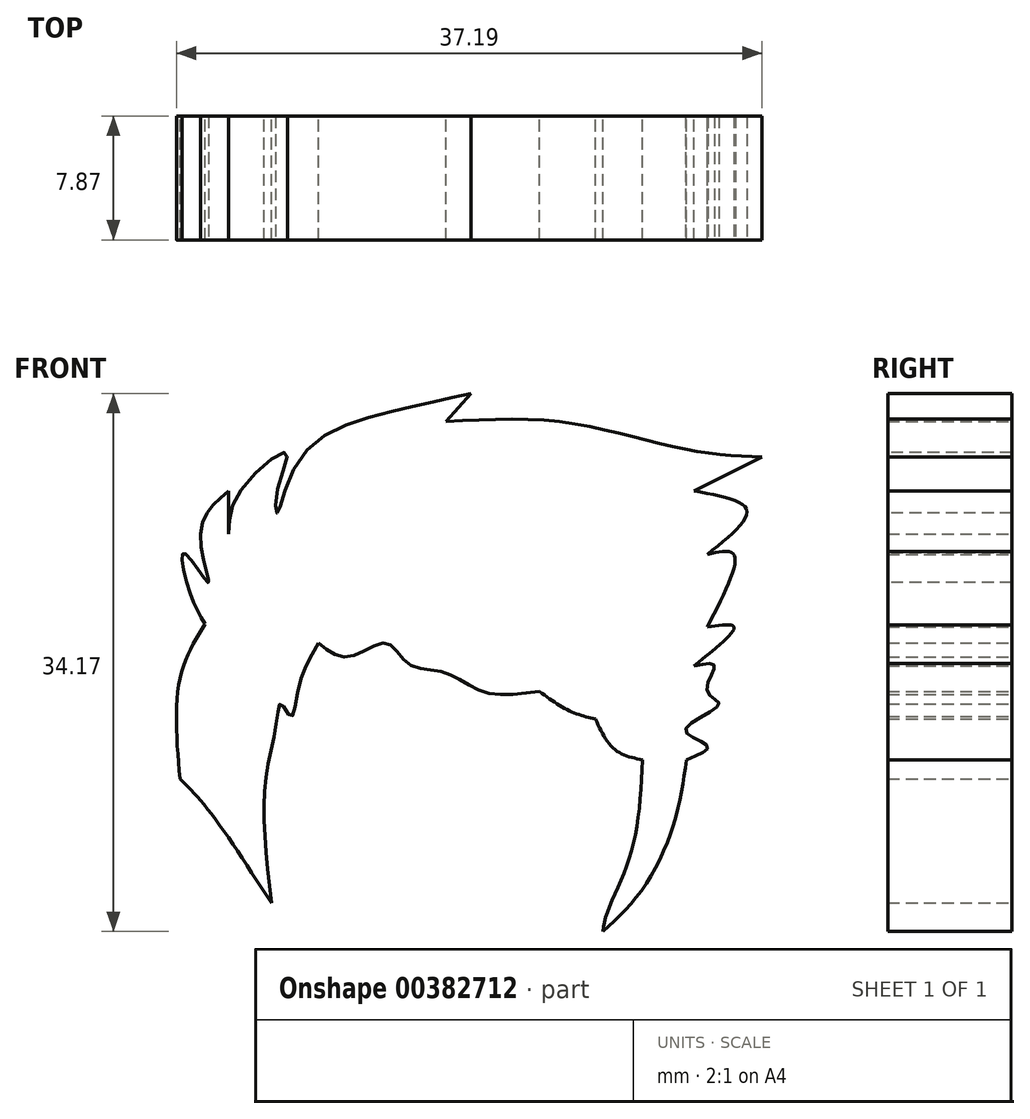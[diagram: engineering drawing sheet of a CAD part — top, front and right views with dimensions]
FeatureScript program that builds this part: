
annotation { "Feature Type Name" : "Feature", "Feature Type Description" : "" }
export const myFeature = defineFeature(function(context is Context, id is Id, definition is map)
    precondition{}
    {
        {
            var Q0;
            Q0=qCreatedBy(makeId("Front.planeOp"),FACE);
            var sketch = newSketch(context, id + "F0", { "sketchPlane" : qUnion([Q0])});
            skFitSpline(sketch, "E0", {"points": [v(-99.37, 25.37) * mm, v(-100.4, 27.63) * mm, v(-100.68, 29.88) * mm, v(-99.18, 28) * mm, v(-99.65, 31) * mm, v(-97.86, 33.82) * mm], "startDerivative": vector(-5.52, 9.55) * mm, "endDerivative": vector(11.78, 9.9) * mm});
            skFitSpline(sketch, "E1", {"points": [v(-97.86, 31.1) * mm, v(-97.86, 33.82) * mm], "startDerivative": vector(0, 2.72) * mm, "endDerivative": vector(0, 2.72) * mm});
            skFitSpline(sketch, "E2", {"points": [v(-97.86, 31.1) * mm, v(-97.11, 33.82) * mm, v(-94.2, 36.26) * mm, v(-94.77, 33.82) * mm, v(-94.77, 32.41) * mm, v(-93.27, 35.98) * mm, v(-87.45, 38.89) * mm, v(-82.48, 40.01) * mm], "startDerivative": vector(0.53, 19.9) * mm, "endDerivative": vector(27.38, 6.02) * mm});
            skFitSpline(sketch, "E3", {"points": [v(-84.07, 38.23) * mm, v(-82.48, 40.01) * mm], "startDerivative": vector(1.6, 1.78) * mm, "endDerivative": vector(1.6, 1.78) * mm});
            skFitSpline(sketch, "E4", {"points": [v(-84.07, 38.23) * mm, v(-76.94, 38.23) * mm, v(-71.22, 37) * mm, v(-67, 36.16) * mm, v(-63.99, 35.98) * mm], "startDerivative": vector(24.35, 1.27) * mm, "endDerivative": vector(14.89, -0.43) * mm});
            skFitSpline(sketch, "E5", {"points": [v(-68.3, 33.82) * mm, v(-63.99, 35.98) * mm], "startDerivative": vector(4.32, 2.16) * mm, "endDerivative": vector(4.32, 2.16) * mm});
            skFitSpline(sketch, "E6", {"points": [v(-68.3, 33.82) * mm, v(-64.96, 32.6) * mm, v(-67.46, 29.78) * mm], "startDerivative": vector(9.69, -1.71) * mm, "endDerivative": vector(-7.92, -6.33) * mm});
            skFitSpline(sketch, "E7", {"points": [v(-67.46, 29.78) * mm, v(-65.77, 29.78) * mm, v(-67.46, 25.19) * mm], "startDerivative": vector(5.9, 1.35) * mm, "endDerivative": vector(-4.96, -9.6) * mm});
            skFitSpline(sketch, "E8", {"points": [v(-99.37, 25.37) * mm, v(-100.96, 21.9) * mm, v(-100.96, 15.52) * mm], "startDerivative": vector(-4.45, -7.23) * mm, "endDerivative": vector(1.03, -12.27) * mm});
            skFitSpline(sketch, "E9", {"points": [v(-100.96, 15.52) * mm, v(-99.37, 13.83) * mm, v(-95.14, 7.64) * mm], "startDerivative": vector(4.08, -3.84) * mm, "endDerivative": vector(7.25, -11.22) * mm});
            skFitSpline(sketch, "E10", {"points": [v(-95.14, 7.64) * mm, v(-95.59, 12.45) * mm, v(-95.42, 16.04) * mm, v(-94.81, 19.16) * mm, v(-94.53, 20.29) * mm, v(-93.9, 19.5) * mm, v(-93.43, 21.32) * mm, v(-92.17, 24.16) * mm], "startDerivative": vector(-2.88, 25.1) * mm, "endDerivative": vector(9.57, 16.24) * mm});
            skFitSpline(sketch, "E11", {"points": [v(-92.17, 24.16) * mm, v(-90.2, 23.29) * mm, v(-87.9, 24.16) * mm, v(-86.4, 22.81) * mm, v(-84.07, 22.26) * mm, v(-81.75, 21.08) * mm, v(-78.12, 21.08) * mm], "startDerivative": vector(12.13, -9.64) * mm, "endDerivative": vector(19.59, 2.52) * mm});
            skFitSpline(sketch, "E12", {"points": [v(-78.12, 21.08) * mm, v(-76.15, 19.82) * mm, v(-74.57, 19.34) * mm], "startDerivative": vector(3.67, -2.67) * mm, "endDerivative": vector(3.42, -0.75) * mm});
            skFitSpline(sketch, "E13", {"points": [v(-74.57, 19.34) * mm, v(-73.3, 17.37) * mm, v(-71.57, 16.74) * mm], "startDerivative": vector(2.04, -4.36) * mm, "endDerivative": vector(4, -0.78) * mm});
            skFitSpline(sketch, "E14", {"points": [v(-71.57, 16.74) * mm, v(-71.98, 12.27) * mm, v(-72.9, 9.18) * mm, v(-73.84, 7) * mm, v(-74.1, 5.84) * mm], "startDerivative": vector(-0.74, -14.44) * mm, "endDerivative": vector(-1.03, -6.47) * mm});
            skFitSpline(sketch, "E15", {"points": [v(-74.1, 5.84) * mm, v(-71.57, 8.53) * mm, v(-69.52, 12.88) * mm, v(-68.8, 16.74) * mm], "startDerivative": vector(8.36, 7.62) * mm, "endDerivative": vector(1.5, 11.56) * mm});
            skFitSpline(sketch, "E16", {"points": [v(-67.46, 25.19) * mm, v(-65.77, 25.19) * mm, v(-68.3, 22.7) * mm], "startDerivative": vector(5.86, 0.86) * mm, "endDerivative": vector(-6.77, -5.44) * mm});
            skFitSpline(sketch, "E17", {"points": [v(-68.3, 22.7) * mm, v(-67, 22.7) * mm, v(-67.46, 21.08) * mm, v(-66.73, 20.25) * mm, v(-68.85, 18.63) * mm, v(-67.46, 17.63) * mm, v(-68.8, 16.74) * mm], "startDerivative": vector(12.6, 2.73) * mm, "endDerivative": vector(-13.9, -5.43) * mm});
            skFitSpline(sketch, "E18", {"points": [v(-100.96, 15.52) * mm, v(-101.71, 14.27) * mm, v(-101.43, 10.43) * mm, v(-98.33, 7.64) * mm, v(-96.46, 6.9) * mm], "startDerivative": vector(-4.66, -5.46) * mm, "endDerivative": vector(8.02, -2.52) * mm});
            skFitSpline(sketch, "E19", {"points": [v(-96.46, 6.9) * mm, v(-95.14, 4.98) * mm, v(-92.7, 2.73) * mm, v(-89.7, 1) * mm], "startDerivative": vector(3.97, -6.5) * mm, "endDerivative": vector(8.6, -4.44) * mm});
            skFitSpline(sketch, "E20", {"points": [v(-89.7, 1) * mm, v(-88.2, 1) * mm], "startDerivative": vector(1.5, 0) * mm, "endDerivative": vector(1.5, 0) * mm});
            skFitSpline(sketch, "E21", {"points": [v(-74.1, 5.84) * mm, v(-75.02, 3.76) * mm, v(-77.27, 1) * mm, v(-79.33, 0) * mm], "startDerivative": vector(-2.37, -6.4) * mm, "endDerivative": vector(-6.7, -2.24) * mm});
            skFitSpline(sketch, "E22", {"points": [v(-79.33, 0) * mm, v(-80.08, 1) * mm], "startDerivative": vector(-0.75, 1) * mm, "endDerivative": vector(-0.75, 1) * mm});
            skFitSpline(sketch, "E23", {"points": [v(-88.2, 1) * mm, v(-88.2, 0.38) * mm, v(-86.46, -0.46) * mm, v(-82.48, -0.5) * mm, v(-80.7, 0) * mm, v(-80.08, 1) * mm], "startDerivative": vector(-1.34, -5.24) * mm, "endDerivative": vector(2.85, 6.86) * mm});
            skFitSpline(sketch, "E24", {"points": [v(-84.59, 17.13) * mm, v(-85.67, 16.34) * mm, v(-88.2, 16.74) * mm, v(-90.55, 18.21) * mm, v(-92.17, 18.96) * mm], "startDerivative": vector(-4.47, -4.95) * mm, "endDerivative": vector(-6.84, 2.65) * mm});
            skFitSpline(sketch, "E25", {"points": [v(-84.59, 17.13) * mm, v(-86.93, 18.07) * mm, v(-87.82, 18.17) * mm, v(-92.17, 18.96) * mm], "startDerivative": vector(-7.9, 3.54) * mm, "endDerivative": vector(-11.6, 2.37) * mm});
            skFitSpline(sketch, "E26", {"points": [v(-81.12, 14.5) * mm, v(-79.33, 13.52) * mm, v(-76.52, 13.43) * mm, v(-75.3, 14.18) * mm, v(-74.1, 14.23) * mm], "startDerivative": vector(5.88, -4.24) * mm, "endDerivative": vector(6.27, -0.73) * mm});
            skFitSpline(sketch, "E27", {"points": [v(-81.12, 14.5) * mm, v(-74.1, 14.23) * mm], "startDerivative": vector(7.02, -0.28) * mm, "endDerivative": vector(7.02, -0.28) * mm});
            skFitSpline(sketch, "E28", {"points": [v(-84.89, 13.4) * mm, v(-86.56, 14.23) * mm, v(-88.34, 14.88) * mm, v(-91.01, 15.4) * mm, v(-94.36, 15.06) * mm, v(-95.46, 14.5) * mm], "startDerivative": vector(-8.97, 4.64) * mm, "endDerivative": vector(-5.93, -3.97) * mm});
            skFitSpline(sketch, "E29", {"points": [v(-95.46, 14.5) * mm, v(-95.14, 14.5) * mm, v(-93.05, 14.28) * mm], "startDerivative": vector(0.88, 0.04) * mm, "endDerivative": vector(3.54, -0.44) * mm});
            skFitSpline(sketch, "E30", {"points": [v(-84.89, 13.4) * mm, v(-86.27, 13.4) * mm, v(-87.38, 13.57) * mm], "startDerivative": vector(-2.7, -0.1) * mm, "endDerivative": vector(-2.28, 0.43) * mm});
            skFitSpline(sketch, "E31", {"points": [v(-93.05, 14.28) * mm, v(-92.88, 13.4) * mm, v(-91.74, 12.32) * mm, v(-90.36, 11.73) * mm, v(-88.2, 12.06) * mm, v(-87.4, 12.88) * mm, v(-87.38, 13.57) * mm], "startDerivative": vector(0.07, -6.3) * mm, "endDerivative": vector(-0.73, 5.6) * mm});
            skFitSpline(sketch, "E32", {"points": [v(-95.25, 14.51) * mm, v(-94.7, 13.61) * mm, v(-94.14, 12.97) * mm, v(-91.53, 11.8) * mm, v(-89.16, 11.53) * mm, v(-86.54, 12.32) * mm, v(-84.89, 13.4) * mm], "startDerivative": vector(4.55, -7.7) * mm, "endDerivative": vector(8.77, 6.63) * mm});
            skFitSpline(sketch, "E33", {"points": [v(-81.67, 11.35) * mm, v(-79.47, 12.36) * mm, v(-75.86, 12.38) * mm, v(-74.38, 12.23) * mm, v(-72.65, 11.34) * mm], "startDerivative": vector(7.54, 4.85) * mm, "endDerivative": vector(7.87, -4.77) * mm});
            skFitSpline(sketch, "E34", {"points": [v(-72.65, 11.34) * mm, v(-74.17, 11.46) * mm, v(-75.26, 11.5) * mm], "startDerivative": vector(-2.92, 0.27) * mm, "endDerivative": vector(-2.28, 0.06) * mm});
            skFitSpline(sketch, "E35", {"points": [v(-81.67, 11.35) * mm, v(-80.45, 11.34) * mm], "startDerivative": vector(1.23, -0.01) * mm, "endDerivative": vector(1.23, -0.01) * mm});
            skFitSpline(sketch, "E36", {"points": [v(-80.45, 11.34) * mm, v(-80.3, 10.67) * mm, v(-78.87, 9.83) * mm, v(-76.8, 9.83) * mm, v(-75.65, 10.56) * mm, v(-75.26, 11.5) * mm], "startDerivative": vector(0.07, -4.67) * mm, "endDerivative": vector(1.5, 5.66) * mm});
            skFitSpline(sketch, "E37", {"points": [v(-87.62, 4.84) * mm, v(-81.8, 5.34) * mm], "startDerivative": vector(5.82, 0.5) * mm, "endDerivative": vector(5.82, 0.5) * mm});
            skFitSpline(sketch, "E38", {"points": [v(-87.62, 4.84) * mm, v(-86.83, 4.03) * mm, v(-84.03, 3.3) * mm, v(-82.38, 4.33) * mm, v(-81.8, 5.34) * mm], "startDerivative": vector(2.8, -4) * mm, "endDerivative": vector(2.24, 4.81) * mm});
            skFitSpline(sketch, "E39", {"points": [v(-89.7, 1) * mm, v(-91.58, 0.63) * mm], "startDerivative": vector(-1.88, -0.36) * mm, "endDerivative": vector(-1.88, -0.36) * mm});
            skFitSpline(sketch, "E40", {"points": [v(-90.54, -0.97) * mm, v(-91.3, -0.16) * mm, v(-91.58, 0.63) * mm], "startDerivative": vector(-1.64, 1.47) * mm, "endDerivative": vector(-0.41, 1.74) * mm});
            skFitSpline(sketch, "E41", {"points": [v(-90.54, -0.97) * mm, v(-91.58, -1.28) * mm, v(-92.37, -1.47) * mm], "startDerivative": vector(-2, -0.61) * mm, "endDerivative": vector(-1.64, -0.38) * mm});
            skFitSpline(sketch, "E42", {"points": [v(-92.37, -1.47) * mm, v(-94.05, -3.67) * mm, v(-94.02, -5.97) * mm, v(-94.12, -12.09) * mm, v(-94.27, -17.63) * mm, v(-94.4, -24.78) * mm], "startDerivative": vector(-13.9, -14.17) * mm, "endDerivative": vector(-0.6, -29.87) * mm});
            skFitSpline(sketch, "E43", {"points": [v(-79.33, 0) * mm, v(-78.64, -0.49) * mm, v(-79.33, -0.97) * mm, v(-79.87, -1.47) * mm], "startDerivative": vector(3.12, -1.43) * mm, "endDerivative": vector(-1.33, -1.6) * mm});
            skFitSpline(sketch, "E44", {"points": [v(-79.87, -1.47) * mm, v(-77.64, -1.47) * mm], "startDerivative": vector(2.22, 0) * mm, "endDerivative": vector(2.22, 0) * mm});
            skFitSpline(sketch, "E45", {"points": [v(-77.64, -1.47) * mm, v(-70.11, -12.17) * mm], "startDerivative": vector(7.53, -10.7) * mm, "endDerivative": vector(7.53, -10.7) * mm});
            skFitSpline(sketch, "E46", {"points": [v(-70.11, -12.17) * mm, v(-72.97, -17.8) * mm], "startDerivative": vector(-2.86, -5.64) * mm, "endDerivative": vector(-2.86, -5.64) * mm});
            skFitSpline(sketch, "E47", {"points": [v(-78.64, -6.68) * mm, v(-74.08, -13.1) * mm], "startDerivative": vector(4.56, -6.42) * mm, "endDerivative": vector(4.56, -6.42) * mm});
            skFitSpline(sketch, "E48", {"points": [v(-74.08, -13.1) * mm, v(-76.22, -17.03) * mm, v(-76.22, -18.4) * mm], "startDerivative": vector(-4.4, -6.84) * mm, "endDerivative": vector(0.6, -3.44) * mm});
            skFitSpline(sketch, "E49", {"points": [v(-72.97, -17.8) * mm, v(-74.08, -17.8) * mm, v(-76.22, -18.4) * mm], "startDerivative": vector(-2.48, 0.21) * mm, "endDerivative": vector(-2.2, -4.84) * mm});
            skFitSpline(sketch, "E50", {"points": [v(-76.22, -18.4) * mm, v(-76.22, -18.76) * mm, v(-75.07, -18.4) * mm, v(-73.34, -18.4) * mm, v(-72.97, -17.8) * mm], "startDerivative": vector(-0.68, -3.07) * mm, "endDerivative": vector(1, 3.48) * mm});
            skFitSpline(sketch, "E51", {"points": [v(-76.22, -18.76) * mm, v(-76.22, -19.97) * mm, v(-74.37, -22) * mm], "startDerivative": vector(-0.61, -2.96) * mm, "endDerivative": vector(4, -3.47) * mm});
            skFitSpline(sketch, "E52", {"points": [v(-74.61, -20.67) * mm, v(-73.98, -21.72) * mm, v(-73.98, -22.12) * mm, v(-74.37, -22) * mm], "startDerivative": vector(1.7, -2.37) * mm, "endDerivative": vector(-1.78, 0.93) * mm});
            skFitSpline(sketch, "E53", {"points": [v(-74.61, -20.67) * mm, v(-73.61, -21.72) * mm, v(-73.28, -21.8) * mm, v(-73.32, -21.53) * mm, v(-73.98, -20.45) * mm], "startDerivative": vector(2.97, -3.74) * mm, "endDerivative": vector(-2.47, 3.69) * mm});
            skFitSpline(sketch, "E54", {"points": [v(-73.98, -20.45) * mm, v(-73.23, -21.25) * mm, v(-72.8, -21.33) * mm, v(-72.78, -21.02) * mm, v(-73.71, -19.94) * mm], "startDerivative": vector(2.39, -3.18) * mm, "endDerivative": vector(-3.5, 3.4) * mm});
            skFitSpline(sketch, "E55", {"points": [v(-73.71, -19.94) * mm, v(-73.09, -20.33) * mm, v(-72.73, -20.22) * mm], "startDerivative": vector(1.13, -0.95) * mm, "endDerivative": vector(0.81, 0.47) * mm});
            skFitSpline(sketch, "E56", {"points": [v(-73.34, -18.4) * mm, v(-73.34, -19.06) * mm, v(-72.73, -19.94) * mm, v(-72.73, -20.22) * mm], "startDerivative": vector(-0.45, -1.84) * mm, "endDerivative": vector(-0.33, -1.1) * mm});
            skFitSpline(sketch, "E57", {"points": [v(-84.6, -0.62) * mm, v(-85.5, -1.26) * mm, v(-87.98, -1.32) * mm], "startDerivative": vector(-1.89, -1.9) * mm, "endDerivative": vector(-4.7, 0.35) * mm});
            skFitSpline(sketch, "E58", {"points": [v(-83.41, -0.59) * mm, v(-83.6, -1.5) * mm, v(-83.23, -2.05) * mm, v(-81.87, -2.26) * mm], "startDerivative": vector(-0.96, -2.96) * mm, "endDerivative": vector(3.94, -0.14) * mm});
            skFitSpline(sketch, "E59", {"points": [v(-81.87, -2.26) * mm, v(-82.26, -3.05) * mm, v(-82.14, -5.29) * mm, v(-80.18, -11.82) * mm], "startDerivative": vector(-2.5, -3.75) * mm, "endDerivative": vector(4.68, -14) * mm});
            skFitSpline(sketch, "E60", {"points": [v(-87.98, -1.32) * mm, v(-87.26, -3.93) * mm, v(-85.02, -11.8) * mm, v(-83.47, -16.09) * mm], "startDerivative": vector(2.46, -8.67) * mm, "endDerivative": vector(4.53, -11.62) * mm});
            skFitSpline(sketch, "E61", {"points": [v(-87.9, -1.63) * mm, v(-85.75, -3.35) * mm, v(-85.32, -4.22) * mm], "startDerivative": vector(4.13, -2.88) * mm, "endDerivative": vector(0.74, -2.25) * mm});
            skFitSpline(sketch, "E62", {"points": [v(-86.95, -5.03) * mm, v(-86.26, -4.27) * mm, v(-85.32, -4.22) * mm], "startDerivative": vector(1.21, 1.85) * mm, "endDerivative": vector(2.07, -0.24) * mm});
            skFitSpline(sketch, "E63", {"points": [v(-82.8, -2.2) * mm, v(-83.87, -3.28) * mm, v(-84.45, -4.42) * mm], "startDerivative": vector(-2.27, -2) * mm, "endDerivative": vector(-1.02, -2.47) * mm});
            skFitSpline(sketch, "E64", {"points": [v(-85.5, -3.76) * mm, v(-84.86, -4) * mm, v(-84.45, -4.42) * mm], "startDerivative": vector(1.33, -0.34) * mm, "endDerivative": vector(0.75, -1) * mm});
            skFitSpline(sketch, "E65", {"points": [v(-87.78, -27.12) * mm, v(-85.32, -21.72) * mm, v(-83.47, -16.09) * mm, v(-78.64, -10.35) * mm], "startDerivative": vector(8.68, 16.55) * mm, "endDerivative": vector(15.7, 15.43) * mm});
            skFitSpline(sketch, "E66", {"points": [v(-78.64, -10.35) * mm, v(-77.58, -10.35) * mm, v(-76.22, -21.72) * mm, v(-75.13, -27.2) * mm], "startDerivative": vector(7.56, 3.27) * mm, "endDerivative": vector(3.6, -12.04) * mm});
            skFitSpline(sketch, "E67", {"points": [v(-81.33, -13.1) * mm, v(-81.87, -16.09) * mm, v(-79.8, -26.38) * mm, v(-79.08, -28.16) * mm], "startDerivative": vector(-3.24, -8.25) * mm, "endDerivative": vector(2.8, -5.64) * mm});
            skFitSpline(sketch, "E68", {"points": [v(-75.13, -27.2) * mm, v(-77, -26.74) * mm, v(-79.08, -28.16) * mm], "startDerivative": vector(-4.03, 1.83) * mm, "endDerivative": vector(-3.88, -3.64) * mm});
            skFitSpline(sketch, "E69", {"points": [v(-87.47, -26.54) * mm, v(-86.71, -27.75) * mm, v(-84.45, -28.92) * mm, v(-81.87, -28.92) * mm, v(-80.18, -28.16) * mm, v(-79.08, -28.16) * mm], "startDerivative": vector(3.33, -7.18) * mm, "endDerivative": vector(6.97, -1.04) * mm});
            skFitSpline(sketch, "E70", {"points": [v(-87.78, -27.12) * mm, v(-89.66, -22.29) * mm, v(-90.48, -14.57) * mm], "startDerivative": vector(-4.8, 10) * mm, "endDerivative": vector(-0.73, 14.93) * mm});
            skFitSpline(sketch, "E71", {"points": [v(-91.2, -25.35) * mm, v(-90.08, -19.97) * mm], "startDerivative": vector(1.11, 5.38) * mm, "endDerivative": vector(1.11, 5.38) * mm});
            skFitSpline(sketch, "E72", {"points": [v(-94.4, -24.78) * mm, v(-92.95, -24.98) * mm, v(-91.2, -25.35) * mm], "startDerivative": vector(3, -0.36) * mm, "endDerivative": vector(3.42, -0.78) * mm});
            skFitSpline(sketch, "E73", {"points": [v(-94.4, -24.78) * mm, v(-94.75, -25.62) * mm, v(-94.75, -26.1) * mm, v(-94.4, -26.3) * mm, v(-93.45, -26.2) * mm, v(-93, -26) * mm, v(-92.3, -26.3) * mm, v(-91.47, -26.56) * mm, v(-91.2, -26.13) * mm, v(-91.2, -25.35) * mm], "startDerivative": vector(-3.22, -6.71) * mm, "endDerivative": vector(-0.58, 6.68) * mm});
            skFitSpline(sketch, "E74", {"points": [v(-94.75, -26.1) * mm, v(-94.75, -26.66) * mm, v(-96.11, -27.2) * mm, v(-97.33, -28.16) * mm, v(-96.95, -28.35) * mm, v(-95.75, -28.16) * mm], "startDerivative": vector(1.07, -4.16) * mm, "endDerivative": vector(5.77, 1.42) * mm});
            skFitSpline(sketch, "E75", {"points": [v(-92.86, -27.75) * mm, v(-93.86, -28.16) * mm, v(-95.58, -28.44) * mm, v(-95.75, -28.16) * mm], "startDerivative": vector(-2.34, -1.1) * mm, "endDerivative": vector(-0.34, 1.73) * mm});
            skFitSpline(sketch, "E76", {"points": [v(-92.86, -27.75) * mm, v(-92.28, -28.16) * mm, v(-91.55, -28.16) * mm, v(-91.62, -27.75) * mm, v(-92, -27.45) * mm, v(-91.96, -26.48) * mm], "startDerivative": vector(2.32, -2.24) * mm, "endDerivative": vector(1, 4.76) * mm});
            skFitSpline(sketch, "E77", {"points": [v(-75.67, -25.22) * mm, v(-73.98, -25.35) * mm], "startDerivative": vector(1.7, -0.14) * mm, "endDerivative": vector(1.7, -0.14) * mm});
            skFitSpline(sketch, "E78", {"points": [v(-73.98, -25.35) * mm, v(-71.36, -22.29) * mm, v(-67.24, -16.09) * mm, v(-65.5, -12.68) * mm, v(-66.68, -11.26) * mm, v(-70.11, -12.17) * mm], "startDerivative": vector(12.37, 13.14) * mm, "endDerivative": vector(-19.94, -9.08) * mm});
            skFitSpline(sketch, "E79", {"points": [v(-78.64, -6.68) * mm, v(-78, -8.58) * mm, v(-74.76, -14.17) * mm], "startDerivative": vector(1.24, -4.69) * mm, "endDerivative": vector(6.07, -9.8) * mm});
            skFitSpline(sketch, "E80", {"points": [v(-79.08, -28.16) * mm, v(-78.88, -28.51) * mm, v(-78.81, -29.3) * mm, v(-78.04, -29.54) * mm, v(-75.11, -29.28) * mm, v(-74.2, -29.12) * mm, v(-74.27, -28.43) * mm, v(-75.05, -27.52) * mm, v(-75.13, -27.2) * mm], "startDerivative": vector(3.14, -3.4) * mm, "endDerivative": vector(-0.08, 3.98) * mm});
            skFitSpline(sketch, "E81", {"points": [v(-73.98, -25.35) * mm, v(-73.98, -26.26) * mm, v(-72.43, -27.34) * mm, v(-72.45, -28.16) * mm, v(-73.14, -28.51) * mm, v(-74.12, -28.68) * mm, v(-74.15, -28.71) * mm], "startDerivative": vector(-1.74, -5.38) * mm, "endDerivative": vector(-0.35, -0.84) * mm});
            skFitSpline(sketch, "E82", {"points": [v(-33.6, 29.32) * mm, v(-36.7, 33.01) * mm, v(-41.3, 35.62) * mm, v(-45.53, 36.04) * mm, v(-47.46, 36.34) * mm, v(-48.67, 36.34) * mm, v(-51.88, 35.86) * mm, v(-54.79, 35.56) * mm, v(-59.5, 31.68) * mm, v(-62.4, 26.48) * mm, v(-64.04, 22.37) * mm, v(-64.04, 18.43) * mm, v(-63.38, 16.44) * mm, v(-63.26, 16.86) * mm, v(-63.07, 13.9) * mm, v(-62.77, 13.65) * mm, v(-62.05, 15.17) * mm, v(-61.68, 14.32) * mm, v(-61.68, 12.8) * mm, v(-61.44, 11.66) * mm, v(-60.84, 12.75) * mm, v(-60.84, 14.32) * mm], "startDerivative": vector(-41.78, 57.92) * mm, "endDerivative": vector(-5.65, 38.87) * mm});
            skFitSpline(sketch, "E83", {"points": [v(-33.6, 29.32) * mm, v(-32.58, 28.54) * mm, v(-31.85, 27.02) * mm, v(-33.13, 26.66) * mm, v(-31.98, 26.12) * mm, v(-31.07, 26.36) * mm, v(-32.28, 24.66) * mm, v(-33.6, 19.82) * mm, v(-32.46, 15.1) * mm, v(-32.1, 12.02) * mm], "startDerivative": vector(11.09, -6.68) * mm, "endDerivative": vector(0.98, -22.23) * mm});
            skFitSpline(sketch, "E84", {"points": [v(-60.84, 14.32) * mm, v(-57.93, 15.77) * mm, v(-55.63, 17.59) * mm, v(-54.72, 18.67) * mm], "startDerivative": vector(7.7, 3.4) * mm, "endDerivative": vector(3.05, 4.09) * mm});
            skFitSpline(sketch, "E85", {"points": [v(-56.29, 16.98) * mm, v(-57.02, 15.77) * mm], "startDerivative": vector(-0.74, -1.21) * mm, "endDerivative": vector(-0.74, -1.21) * mm});
            skFitSpline(sketch, "E86", {"points": [v(-57.02, 15.77) * mm, v(-53.76, 16.56) * mm, v(-50.61, 18.33) * mm, v(-50, 18.98) * mm], "startDerivative": vector(8.07, 1.27) * mm, "endDerivative": vector(2.17, 2.9) * mm});
            skFitSpline(sketch, "E87", {"points": [v(-53.27, 15.77) * mm, v(-50, 18.98) * mm], "startDerivative": vector(3.27, 3.2) * mm, "endDerivative": vector(3.27, 3.2) * mm});
            skFitSpline(sketch, "E88", {"points": [v(-46.44, 17.59) * mm, v(-48.67, 15.77) * mm, v(-53.27, 15.77) * mm], "startDerivative": vector(-4.37, -5.02) * mm, "endDerivative": vector(-9.12, 1.15) * mm});
            skFitSpline(sketch, "E89", {"points": [v(-39.24, 19.76) * mm, v(-41.66, 17.1) * mm, v(-44.62, 15.17) * mm, v(-47.83, 15.29) * mm], "startDerivative": vector(-6.74, -7.96) * mm, "endDerivative": vector(-10.17, 1.83) * mm});
            skFitSpline(sketch, "E90", {"points": [v(-46.44, 17.59) * mm, v(-47.83, 15.29) * mm], "startDerivative": vector(-1.4, -2.3) * mm, "endDerivative": vector(-1.4, -2.3) * mm});
            skFitSpline(sketch, "E91", {"points": [v(-37.9, 17.59) * mm, v(-39.96, 16.68) * mm, v(-42.45, 16.4) * mm], "startDerivative": vector(-4.08, -2.18) * mm, "endDerivative": vector(-4.99, -0.24) * mm});
            skFitSpline(sketch, "E92", {"points": [v(-37.9, 17.59) * mm, v(-41, 15.1) * mm, v(-39.78, 14.32) * mm], "startDerivative": vector(-7.5, -4.6) * mm, "endDerivative": vector(4.76, -1.7) * mm});
            skFitSpline(sketch, "E93", {"points": [v(-35.85, 15.4) * mm, v(-37.9, 14.32) * mm, v(-39.78, 14.32) * mm], "startDerivative": vector(-3.89, -2.61) * mm, "endDerivative": vector(-3.98, 0.49) * mm});
            skSolve(sketch);
        }
        {
            var Q0;
            Q0=makeQuery(id+"F0.imprint","IMPRINT",FACE,{"disambiguationData":[TD([[makeQuery(id+"F0.imprint","IMPRINT",EDGE,{"derivedFrom":sQuery(id+"F0.wireOp",EDGE,"E0")}),-1.0]])]});
            extrude(context, id + "F1", {"entities" : qUnion([Q0]), "depth" : 7.87 * mm});
        }
    });
